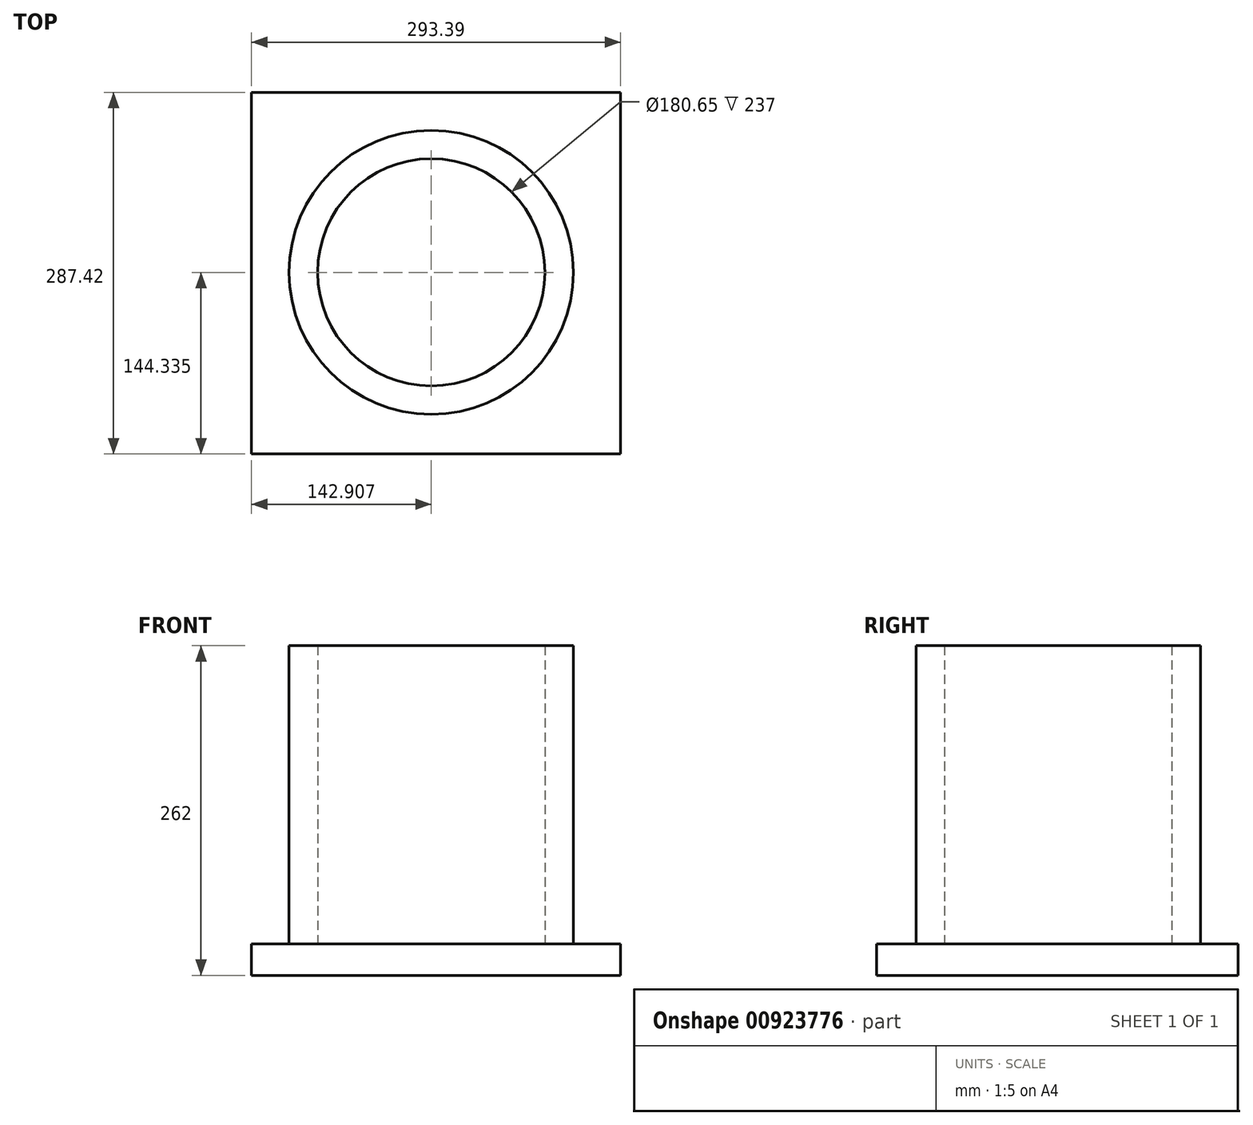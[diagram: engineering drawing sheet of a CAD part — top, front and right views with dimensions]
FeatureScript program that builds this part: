
annotation { "Feature Type Name" : "Feature", "Feature Type Description" : "" }
export const myFeature = defineFeature(function(context is Context, id is Id, definition is map)
    precondition{}
    {
        {
            var Q0;
            Q0=qCreatedBy(makeId("Top.planeOp"),FACE);
            var sketch = newSketch(context, id + "F0", { "sketchPlane" : qUnion([Q0])});
            skCircle(sketch, "E0", {"center": v(29.06, 144.33) * mm, "radius": 112.95 * mm});
            skCircle(sketch, "E1", {"center": v(29.06, 144.33) * mm, "radius": 90.33 * mm});
            skSolve(sketch);
        }
        {
            var Q0;
            Q0 = qSketchRegion(id + "F0", true);
            extrude(context, id + "F1", {"entities" : qUnion([Q0]), "depth" : 175 * mm, "offsetDistance" : 25 * mm});
        }
        {
            var Q0;
            Q0=makeQuery(id+"F1.opExtrude","CAP_FACE",FACE,{"disambiguationData":[OSD([sQuery(id+"F0.wireOp",EDGE,"E0"),sQuery(id+"F0.wireOp",EDGE,"E1")])],"isStart":false});
            extrude(context, id + "F2", {"entities" : qUnion([Q0]), "operationType" : NewBodyOperationType.ADD, "depth" : 87 * mm, "offsetDistance" : 25 * mm});
        }
        {
            var Q0;
            Q0=qCreatedBy(makeId("Top.planeOp"),FACE);
            var sketch = newSketch(context, id + "F3", { "sketchPlane" : qUnion([Q0])});
            skLineSegment(sketch, "E2.bottom", {"start": v(-113.85, 0) * mm, "end": v(179.54, 0) * mm});
            skLineSegment(sketch, "E2.top", {"start": v(-113.85, 287.42) * mm, "end": v(179.54, 287.42) * mm});
            skLineSegment(sketch, "E2.left", {"start": v(-113.85, 0) * mm, "end": v(-113.85, 287.42) * mm});
            skLineSegment(sketch, "E2.right", {"start": v(179.54, 0) * mm, "end": v(179.54, 287.42) * mm});
            skSolve(sketch);
        }
        {
            var Q0;
            Q0 = qSketchRegion(id + "F3", true);
            extrude(context, id + "F4", {"entities" : qUnion([Q0]), "operationType" : NewBodyOperationType.ADD, "depth" : 25 * mm, "offsetDistance" : 25 * mm});
        }
    });
